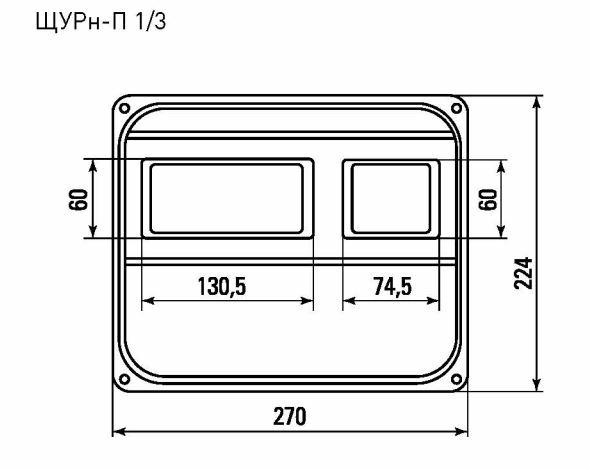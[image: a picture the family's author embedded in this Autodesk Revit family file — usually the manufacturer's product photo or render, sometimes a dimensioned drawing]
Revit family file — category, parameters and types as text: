
# Revit family: EKF_EE_Короб_КЭТ_Для_УЭРМС(1160х300х160)_Basic
name_source: partatom
category: Электрооборудование
units: mm (PartAtom-declared; Revit-internal decimal feet)

## family parameters
Всегда вертикально = Да
На основе рабочей плоскости = Нет
Общий = Нет
При загрузке вырезать с полостями = Нет
Размер круглого соединителя = Использовать диаметр
Тип детали = Силовой щит
Точка расчета площади = Да

## types (1)
- Короб КЭТ для УЭРМС (1160х300х160) EKF Basic
    ADSK_Единица измерения = компл.
    ADSK_Завод-изготовитель = EKF
    ADSK_Классификация нагрузок = Прочее
    ADSK_Код изделия = uerms-01ket
    ADSK_Количество = 1
    ADSK_Количество фаз = 3
    ADSK_Коэффициент мощности = 1
    ADSK_Марка = Короб КЭТ для УЭРМС
    ADSK_Масса = 0
    ADSK_Материал = RAL 7035_Сталь
    ADSK_Наименование = Короб КЭТ для УЭРМС (1160х300х160) EKF BasicКороб КЭТ для УЭРМС (1160х300х160) EKF Basic
    ADSK_Напряжение = 400 В
    ADSK_Номинальная мощность = 0 Вт
    ADSK_Обозначение = Короб КЭТ для УЭРМС
    ADSK_Полная мощность = 0 В·А
    ADSK_Размер_Высота = 1160 мм
    ADSK_Размер_Глубина = 160 мм
    ADSK_Размер_Ширина = 300 мм
    ADSK_Ток = 125 А
    Изготовитель = EKF
    Количество DIN-реек = 0
    Количество модулей на DIN-рейке = 0
    Максимальное количество модулей = 0
    Описание = Короб КЭТ для УЭРМС (1160х300х160) EKF BasicКороб КЭТ для УЭРМС (1160х300х160) EKF Basic
    Серия номенклатуры = Basic
    Степень защиты IP = IP31
    ТВ = EKF
    Тип = 218 мм
    Тип установки = Навесной
